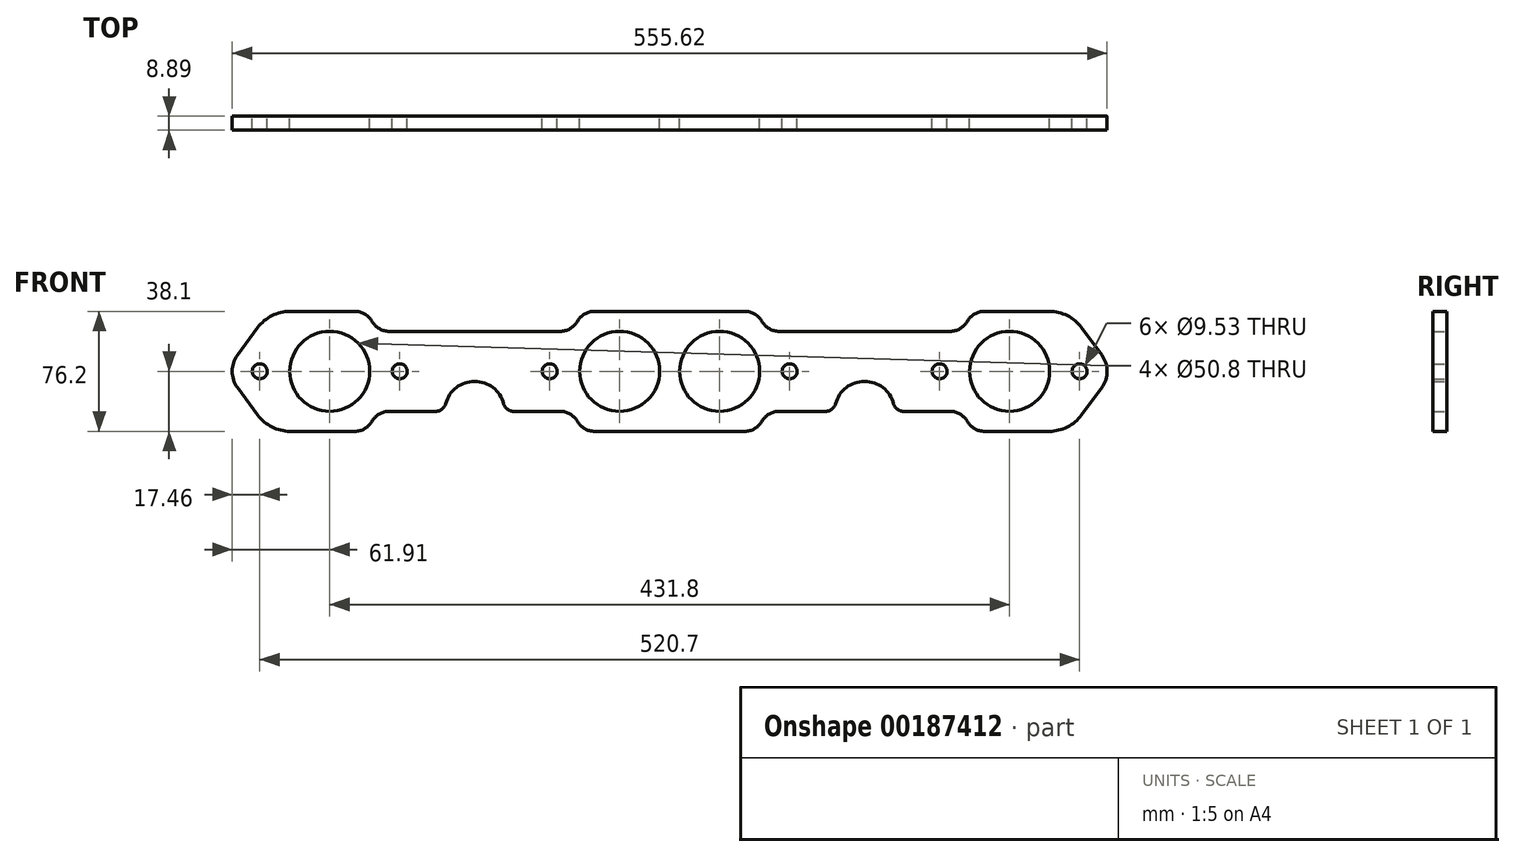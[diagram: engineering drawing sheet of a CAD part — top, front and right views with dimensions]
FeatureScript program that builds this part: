
annotation { "Feature Type Name" : "Feature", "Feature Type Description" : "" }
export const myFeature = defineFeature(function(context is Context, id is Id, definition is map)
    precondition{}
    {
        {
            var Q0;
            Q0=qCreatedBy(makeId("Front.planeOp"),FACE);
            var sketch = newSketch(context, id + "F0", { "sketchPlane" : qUnion([Q0])});
            skLineSegment(sketch, "E0.bottom", {"start": v(-241.15, 38.1) * mm, "end": v(-200.03, 38.1) * mm});
            skLineSegment(sketch, "E0.top", {"start": v(-241.15, -38.1) * mm, "end": v(-200.03, -38.1) * mm});
            skLineSegment(sketch, "E0.left", {"start": v(-254, 38.1) * mm, "end": v(-254, 34.61) * mm});
            skPoint(sketch, "E0.middle", {"position": v(0, 0) * mm});
            skCircle(sketch, "E1", {"center": v(-260.35, 0) * mm, "radius": 4.76 * mm});
            skArc(sketch, "E2.0", {"start": v(-274.42, 10.35) * mm, "mid": v(-277.81, 0) * mm, "end": v(-274.42, -10.35) * mm});
            skLineSegment(sketch, "E3", {"start": v(-261.61, 27.75) * mm, "end": v(-274.42, 10.35) * mm});
            skLineSegment(sketch, "E4.MirrorCS", {"start": v(-261.61, -27.75) * mm, "end": v(-274.42, -10.35) * mm});
            skCircle(sketch, "E5", {"center": v(-215.9, 0) * mm, "radius": 25.4 * mm});
            skCircle(sketch, "E6", {"center": v(-171.45, 0) * mm, "radius": 4.76 * mm});
            skCircle(sketch, "E7", {"center": v(-31.75, 0) * mm, "radius": 25.4 * mm});
            skCircle(sketch, "E8", {"center": v(-76.2, 0) * mm, "radius": 4.76 * mm});
            skLineSegment(sketch, "E9", {"start": v(-178.03, 25.4) * mm, "end": v(-69.62, 25.4) * mm});
            skLineSegment(sketch, "E10", {"start": v(-187.33, 25.4) * mm, "end": v(-187.33, 25.4) * mm});
            skLineSegment(sketch, "E11", {"start": v(-60.33, 25.4) * mm, "end": v(-60.33, 25.4) * mm});
            skLineSegment(sketch, "E12.trimOffspring", {"start": v(-47.62, 38.1) * mm, "end": v(47.62, 38.1) * mm});
            skLineSegment(sketch, "E13.MirrorCS", {"start": v(-178.03, -25.4) * mm, "end": v(-148.42, -25.4) * mm});
            skLineSegment(sketch, "E14.MirrorCS", {"start": v(-187.33, -25.4) * mm, "end": v(-187.33, -25.4) * mm});
            skLineSegment(sketch, "E15.MirrorCS", {"start": v(-60.33, -25.4) * mm, "end": v(-60.33, -25.4) * mm});
            skLineSegment(sketch, "E16.trimOffspring", {"start": v(-47.62, -38.1) * mm, "end": v(47.62, -38.1) * mm});
            skPoint(sketch, "E17.visualSharp", {"position": v(-187.33, 38.1) * mm});
            skArc(sketch, "E17.filletArc", {"start": v(-189.03, 31.75) * mm, "mid": v(-193.67, 36.4) * mm, "end": v(-200.03, 38.1) * mm});
            skPoint(sketch, "E18.visualSharp", {"position": v(-187.33, -38.1) * mm});
            skArc(sketch, "E18.filletArc", {"start": v(-200.03, -38.1) * mm, "mid": v(-193.68, -36.4) * mm, "end": v(-189.03, -31.75) * mm});
            skPoint(sketch, "E19.visualSharp", {"position": v(-187.33, -25.4) * mm});
            skArc(sketch, "E19.filletArc", {"start": v(-178.03, -25.4) * mm, "mid": v(-184.38, -27.1) * mm, "end": v(-189.03, -31.75) * mm});
            skPoint(sketch, "E20.visualSharp", {"position": v(-187.33, 25.4) * mm});
            skArc(sketch, "E20.filletArc", {"start": v(-189.03, 31.75) * mm, "mid": v(-184.38, 27.1) * mm, "end": v(-178.03, 25.4) * mm});
            skPoint(sketch, "E21.visualSharp", {"position": v(-254, 38.1) * mm});
            skArc(sketch, "E21.filletArc", {"start": v(-241.15, 38.1) * mm, "mid": v(-252.62, 35.37) * mm, "end": v(-261.61, 27.75) * mm});
            skPoint(sketch, "E22.visualSharp", {"position": v(-254, -38.1) * mm});
            skArc(sketch, "E22.filletArc", {"start": v(-261.61, -27.75) * mm, "mid": v(-252.62, -35.37) * mm, "end": v(-241.15, -38.1) * mm});
            skPoint(sketch, "E23.visualSharp", {"position": v(-60.33, 38.1) * mm});
            skArc(sketch, "E23.filletArc", {"start": v(-47.62, 38.1) * mm, "mid": v(-53.98, 36.4) * mm, "end": v(-58.62, 31.75) * mm});
            skPoint(sketch, "E24.visualSharp", {"position": v(-60.33, 25.4) * mm});
            skArc(sketch, "E24.filletArc", {"start": v(-69.62, 25.4) * mm, "mid": v(-63.27, 27.1) * mm, "end": v(-58.62, 31.75) * mm});
            skPoint(sketch, "E25.visualSharp", {"position": v(-60.33, -38.1) * mm});
            skArc(sketch, "E25.filletArc", {"start": v(-58.62, -31.75) * mm, "mid": v(-53.98, -36.4) * mm, "end": v(-47.62, -38.1) * mm});
            skPoint(sketch, "E26.visualSharp", {"position": v(-60.33, -25.4) * mm});
            skArc(sketch, "E26.filletArc", {"start": v(-58.62, -31.75) * mm, "mid": v(-63.27, -27.1) * mm, "end": v(-69.62, -25.4) * mm});
            skCircle(sketch, "E27.MirrorC", {"center": v(31.75, 0) * mm, "radius": 25.4 * mm});
            skArc(sketch, "E28.MirrorCS", {"start": v(47.62, 38.1) * mm, "mid": v(53.98, 36.4) * mm, "end": v(58.62, 31.75) * mm});
            skArc(sketch, "E29.MirrorCS", {"start": v(69.62, 25.4) * mm, "mid": v(63.27, 27.1) * mm, "end": v(58.62, 31.75) * mm});
            skLineSegment(sketch, "E30.MirrorCS", {"start": v(178.03, 25.4) * mm, "end": v(69.62, 25.4) * mm});
            skArc(sketch, "E31.MirrorCS", {"start": v(178.03, -25.4) * mm, "mid": v(184.38, -27.1) * mm, "end": v(189.03, -31.75) * mm});
            skArc(sketch, "E32.MirrorCS", {"start": v(58.62, -31.75) * mm, "mid": v(63.27, -27.1) * mm, "end": v(69.62, -25.4) * mm});
            skArc(sketch, "E33.MirrorCS", {"start": v(189.03, 31.75) * mm, "mid": v(184.38, 27.1) * mm, "end": v(178.03, 25.4) * mm});
            skPoint(sketch, "E34.MirrorP", {"position": v(60.33, -25.4) * mm});
            skPoint(sketch, "E35.MirrorP", {"position": v(187.33, 25.4) * mm});
            skPoint(sketch, "E36.MirrorP", {"position": v(187.33, -25.4) * mm});
            skPoint(sketch, "E37.MirrorP", {"position": v(60.33, 25.4) * mm});
            skLineSegment(sketch, "E38.MirrorCS", {"start": v(60.33, 25.4) * mm, "end": v(60.33, 25.4) * mm});
            skLineSegment(sketch, "E39.MirrorCS", {"start": v(261.61, 27.75) * mm, "end": v(274.42, 10.35) * mm});
            skLineSegment(sketch, "E40.MirrorCS", {"start": v(261.61, -27.75) * mm, "end": v(274.42, -10.35) * mm});
            skLineSegment(sketch, "E41.MirrorCS", {"start": v(178.03, -25.4) * mm, "end": v(148.42, -25.4) * mm});
            skCircle(sketch, "E42.MirrorC", {"center": v(215.9, 0) * mm, "radius": 25.4 * mm});
            skArc(sketch, "E43.MirrorCS", {"start": v(274.42, 10.35) * mm, "mid": v(277.81, 0) * mm, "end": v(274.42, -10.35) * mm});
            skCircle(sketch, "E44.MirrorC", {"center": v(260.35, 0) * mm, "radius": 4.76 * mm});
            skArc(sketch, "E45.MirrorCS", {"start": v(58.62, -31.75) * mm, "mid": v(53.98, -36.4) * mm, "end": v(47.62, -38.1) * mm});
            skLineSegment(sketch, "E46.MirrorCS", {"start": v(60.33, -25.4) * mm, "end": v(60.33, -25.4) * mm});
            skLineSegment(sketch, "E47.MirrorCS", {"start": v(187.33, 25.4) * mm, "end": v(187.33, 25.4) * mm});
            skLineSegment(sketch, "E48.MirrorCS", {"start": v(241.15, -38.1) * mm, "end": v(200.03, -38.1) * mm});
            skLineSegment(sketch, "E49.MirrorCS", {"start": v(241.15, 38.1) * mm, "end": v(200.03, 38.1) * mm});
            skLineSegment(sketch, "E50.MirrorCS", {"start": v(187.33, -25.4) * mm, "end": v(187.33, -25.4) * mm});
            skArc(sketch, "E51.MirrorCS", {"start": v(189.03, 31.75) * mm, "mid": v(193.67, 36.4) * mm, "end": v(200.03, 38.1) * mm});
            skArc(sketch, "E52.MirrorCS", {"start": v(241.15, 38.1) * mm, "mid": v(252.62, 35.37) * mm, "end": v(261.61, 27.75) * mm});
            skCircle(sketch, "E53.MirrorC", {"center": v(171.45, 0) * mm, "radius": 4.76 * mm});
            skArc(sketch, "E54.MirrorCS", {"start": v(200.03, -38.1) * mm, "mid": v(193.68, -36.4) * mm, "end": v(189.03, -31.75) * mm});
            skCircle(sketch, "E55.MirrorC", {"center": v(76.2, 0) * mm, "radius": 4.76 * mm});
            skArc(sketch, "E56.MirrorCS", {"start": v(261.61, -27.75) * mm, "mid": v(252.62, -35.37) * mm, "end": v(241.15, -38.1) * mm});
            skLineSegment(sketch, "E57.trimOffspring", {"start": v(-254, -34.61) * mm, "end": v(-254, -38.1) * mm});
            skLineSegment(sketch, "E58.trimOffspring", {"start": v(200.03, 38.1) * mm, "end": v(241.15, 38.1) * mm});
            skLineSegment(sketch, "E59.trimOffspring", {"start": v(200.03, -38.1) * mm, "end": v(241.15, -38.1) * mm});
            skArc(sketch, "E60", {"start": v(-105.38, -20.64) * mm, "mid": v(-123.83, -6.35) * mm, "end": v(-142.27, -20.64) * mm});
            skLineSegment(sketch, "E61.trimOffspring", {"start": v(-99.23, -25.4) * mm, "end": v(-69.62, -25.4) * mm});
            skPoint(sketch, "E62.visualSharp", {"position": v(-142.88, -25.4) * mm});
            skArc(sketch, "E62.filletArc", {"start": v(-148.42, -25.4) * mm, "mid": v(-144.53, -24.07) * mm, "end": v(-142.27, -20.64) * mm});
            skPoint(sketch, "E63.visualSharp", {"position": v(-104.78, -25.4) * mm});
            skArc(sketch, "E63.filletArc", {"start": v(-105.38, -20.64) * mm, "mid": v(-103.12, -24.07) * mm, "end": v(-99.23, -25.4) * mm});
            skArc(sketch, "E64.MirrorCS", {"start": v(105.38, -20.64) * mm, "mid": v(103.12, -24.07) * mm, "end": v(99.23, -25.4) * mm});
            skArc(sketch, "E65.MirrorCS", {"start": v(105.38, -20.64) * mm, "mid": v(123.83, -6.35) * mm, "end": v(142.27, -20.64) * mm});
            skArc(sketch, "E66.MirrorCS", {"start": v(148.42, -25.4) * mm, "mid": v(144.53, -24.07) * mm, "end": v(142.27, -20.64) * mm});
            skLineSegment(sketch, "E67.trimOffspring", {"start": v(99.23, -25.4) * mm, "end": v(69.62, -25.4) * mm});
            skSolve(sketch);
        }
        {
            var Q0;
            {var subQ4=sQuery(id+"F0.wireOp",EDGE,"E0.bottom");Q0=makeQuery(id+"F0.imprint","IMPRINT",FACE,{"disambiguationData":[TD([[makeQuery(id+"F0.imprint","IMPRINT",EDGE,{"derivedFrom":subQ4}),-1.0]])]});}
            extrude(context, id + "F1", {"entities" : qUnion([Q0]), "depth" : 8.9 * mm});
        }
    });
